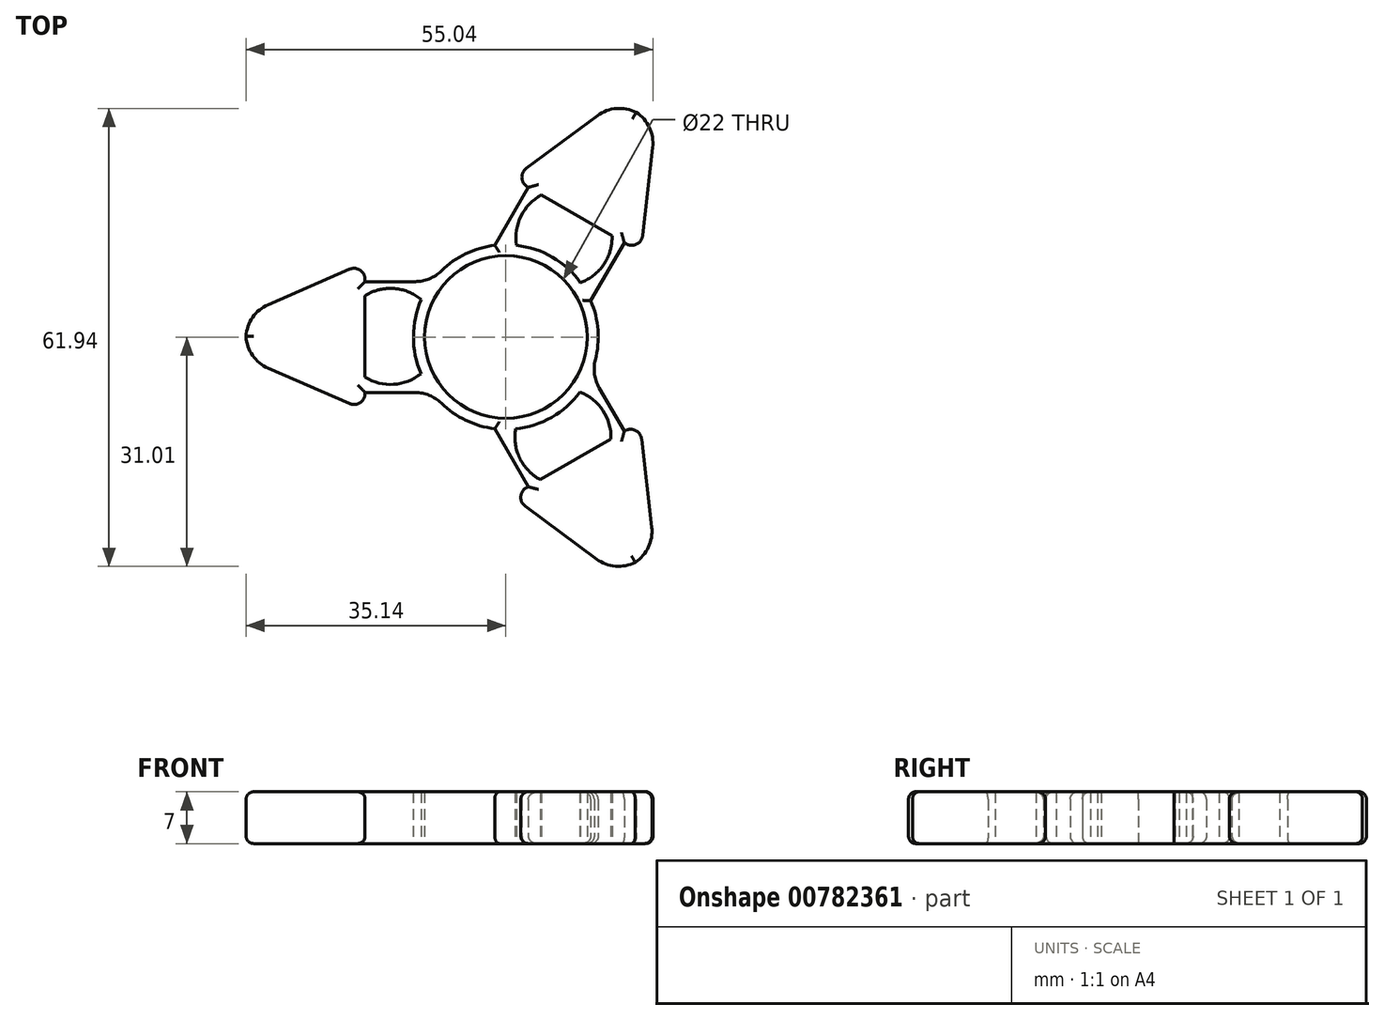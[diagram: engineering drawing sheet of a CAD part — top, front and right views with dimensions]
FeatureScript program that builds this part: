
annotation { "Feature Type Name" : "Feature", "Feature Type Description" : "" }
export const myFeature = defineFeature(function(context is Context, id is Id, definition is map)
    precondition{}
    {
        {
            var Q0;
            Q0=qCreatedBy(makeId("Top.planeOp"),FACE);
            var sketch = newSketch(context, id + "F0", { "sketchPlane" : qUnion([Q0])});
            skArc(sketch, "E0", {"start": v(0, 11) * mm, "mid": v(-11, 0.08) * mm, "end": v(-0.16, -11) * mm});
            skLineSegment(sketch, "E1", {"start": v(0, 11) * mm, "end": v(0, 55) * mm, "construction": true});
            skLineSegment(sketch, "E2", {"start": v(0, -12.5) * mm, "end": v(0, -44.64) * mm, "construction": true});
            skLineSegment(sketch, "E3", {"start": v(0, 55) * mm, "end": v(-40, 55) * mm, "construction": true});
            skLineSegment(sketch, "E4", {"start": v(-40, 55) * mm, "end": v(-40, -44.64) * mm, "construction": true});
            skLineSegment(sketch, "E5", {"start": v(-11, 0.08) * mm, "end": v(-40, 0.08) * mm, "construction": true});
            skLineSegment(sketch, "E6", {"start": v(-35.15, 0.08) * mm, "end": v(-35.15, 3.08) * mm});
            skLineSegment(sketch, "E7", {"start": v(-35.15, 0.08) * mm, "end": v(-35.15, -2.92) * mm});
            skLineSegment(sketch, "E8", {"start": v(-19.05, 0.08) * mm, "end": v(-19.05, 10.08) * mm});
            skLineSegment(sketch, "E9", {"start": v(-19.05, 0.08) * mm, "end": v(-19.05, -9.92) * mm});
            skLineSegment(sketch, "E10", {"start": v(-19.05, 10.08) * mm, "end": v(-35.15, 3.08) * mm});
            skLineSegment(sketch, "E11", {"start": v(-19.05, -9.92) * mm, "end": v(-35.15, -2.92) * mm});
            skLineSegment(sketch, "E12", {"start": v(-8.05, 7.5) * mm, "end": v(-8.05, -7.5) * mm, "construction": true});
            skLineSegment(sketch, "E13", {"start": v(-10, 7.5) * mm, "end": v(-19.05, 7.5) * mm});
            skLineSegment(sketch, "E14", {"start": v(-10, -7.5) * mm, "end": v(-19.05, -7.5) * mm});
            skPoint(sketch, "E15", {"position": v(-15.6, 0.08) * mm});
            skArc(sketch, "E16", {"start": v(-19.05, -5.43) * mm, "mid": v(-15.19, -6.4) * mm, "end": v(-11.48, -4.94) * mm});
            skArc(sketch, "E17.trimOffspring", {"start": v(-11.43, 5.06) * mm, "mid": v(-15.15, 6.57) * mm, "end": v(-19.05, 5.6) * mm});
            skArc(sketch, "E18", {"start": v(0, 12.5) * mm, "mid": v(-5.6, 11.18) * mm, "end": v(-10, 7.5) * mm});
            skLineSegment(sketch, "E19", {"start": v(0, 11) * mm, "end": v(0, 12.5) * mm});
            skArc(sketch, "E20.trimOffspring", {"start": v(-10, -7.5) * mm, "mid": v(-5.6, -11.18) * mm, "end": v(0, -12.5) * mm});
            skArc(sketch, "E21", {"start": v(-11.43, 5.06) * mm, "mid": v(-12.5, 0.07) * mm, "end": v(-11.48, -4.94) * mm});
            skPoint(sketch, "E22.orphan", {"position": v(0, -12.13) * mm});
            skLineSegment(sketch, "E23", {"start": v(-0.16, -11) * mm, "end": v(0, -12.5) * mm});
            skSolve(sketch);
        }
        {
            var Q0;
            Q0=qCreatedBy(makeId("Front.planeOp"),FACE);
            var sketch = newSketch(context, id + "F1", { "sketchPlane" : qUnion([Q0])});
            skLineSegment(sketch, "E24", {"start": v(0, 0) * mm, "end": v(0, 17.47) * mm, "construction": true});
            skSolve(sketch);
        }
        {
            var Q0;
            Q0=makeQuery(id+"F0.imprint","IMPRINT",FACE,{"disambiguationData":[TD([[makeQuery(id+"F0.imprint","IMPRINT",EDGE,{"derivedFrom":sQuery(id+"F0.wireOp",EDGE,"E6")}),-1.0]])]});
            var Q1;
            {var subQ1=sQuery(id+"F0.wireOp",EDGE,"E14");Q1=makeQuery(id+"F0.imprint","IMPRINT",FACE,{"disambiguationData":[TD([[makeQuery(id+"F0.imprint","IMPRINT",EDGE,{"derivedFrom":subQ1}),-1.0]])]});}
            var Q2;
            {var subQ0=sQuery(id+"F0.wireOp",EDGE,"E13");Q2=makeQuery(id+"F0.imprint","IMPRINT",FACE,{"disambiguationData":[TD([[makeQuery(id+"F0.imprint","IMPRINT",EDGE,{"derivedFrom":subQ0}),1.0]])]});}
            extrude(context, id + "F2", {"entities" : qUnion([Q0, Q1, Q2]), "depth" : 7 * mm, "offsetDistance" : 25 * mm});
        }
        {
            var Q0;
            Q0=makeQuery(id+"F2.opExtrude","SWEPT_BODY",BODY,{"disambiguationData":[OSD([sQuery(id+"F0.wireOp",EDGE,"E0"),sQuery(id+"F0.wireOp",EDGE,"E6"),sQuery(id+"F0.wireOp",EDGE,"E7"),sQuery(id+"F0.wireOp",EDGE,"E8"),sQuery(id+"F0.wireOp",EDGE,"E9"),sQuery(id+"F0.wireOp",EDGE,"E10"),sQuery(id+"F0.wireOp",EDGE,"E11"),sQuery(id+"F0.wireOp",EDGE,"E13"),sQuery(id+"F0.wireOp",EDGE,"E14"),sQuery(id+"F0.wireOp",EDGE,"E16"),sQuery(id+"F0.wireOp",EDGE,"E17.trimOffspring"),sQuery(id+"F0.wireOp",EDGE,"E18"),sQuery(id+"F0.wireOp",EDGE,"YHqfrzSo-FMoi-PR9p-TX1y-DZj2c1Ndsbw0"),sQuery(id+"F0.wireOp",EDGE,"E19"),sQuery(id+"F0.wireOp",EDGE,"E20.trimOffspring")])]});
            var Q1;
            Q1=sQuery(id+"F1.wireOp",EDGE,"E24");
            circularPattern(context, id + "F3", {"operationType" : NewBodyOperationType.ADD, "entities" : qUnion([Q0]), "axis" : qUnion([Q1]), "angle" : 240 * degree, "instanceCount" : 3, "equalSpace" : true});
        }
        {
            var Q0;
            Q0=makeQuery(id+"F2.opExtrude","SWEPT_EDGE",EDGE,{"disambiguationData":[OSD([sQuery(id+"F0.wireOp",EDGE,"E9"),sQuery(id+"F0.wireOp",EDGE,"E11")])]});
            var Q1;
            Q1=makeQuery(id+"F3.opPattern","COPY",EDGE,{"derivedFrom":makeQuery(id+"F2.opExtrude","SWEPT_EDGE",EDGE,{"disambiguationData":[OSD([sQuery(id+"F0.wireOp",EDGE,"E8"),sQuery(id+"F0.wireOp",EDGE,"E10")])]}),"instanceName":"1"});
            var Q2;
            Q2=makeQuery(id+"F2.opExtrude","SWEPT_EDGE",EDGE,{"disambiguationData":[OSD([sQuery(id+"F0.wireOp",EDGE,"E8"),sQuery(id+"F0.wireOp",EDGE,"E10")])]});
            var Q3;
            Q3=makeQuery(id+"F3.opPattern","COPY",EDGE,{"derivedFrom":makeQuery(id+"F2.opExtrude","SWEPT_EDGE",EDGE,{"disambiguationData":[OSD([sQuery(id+"F0.wireOp",EDGE,"E9"),sQuery(id+"F0.wireOp",EDGE,"E11")])]}),"instanceName":"1"});
            var Q4;
            Q4=makeQuery(id+"F3.opPattern","COPY",EDGE,{"derivedFrom":makeQuery(id+"F2.opExtrude","SWEPT_EDGE",EDGE,{"disambiguationData":[OSD([sQuery(id+"F0.wireOp",EDGE,"E8"),sQuery(id+"F0.wireOp",EDGE,"E10")])]}),"instanceName":"2"});
            var Q5;
            Q5=makeQuery(id+"F3.opPattern","COPY",EDGE,{"derivedFrom":makeQuery(id+"F2.opExtrude","SWEPT_EDGE",EDGE,{"disambiguationData":[OSD([sQuery(id+"F0.wireOp",EDGE,"E9"),sQuery(id+"F0.wireOp",EDGE,"E11")])]}),"instanceName":"2"});
            fillet(context, id + "F4", {"entities" : qUnion([Q0, Q1, Q2, Q3, Q4, Q5]), "radius" : 1.5 * mm, "tangentPropagation" : true, "allowEdgeOverflow" : false});
        }
        {
            var Q0;
            Q0=makeQuery(id+"F2.opExtrude","SWEPT_EDGE",EDGE,{"disambiguationData":[OSD([sQuery(id+"F0.wireOp",EDGE,"E14"),sQuery(id+"F0.wireOp",EDGE,"E20.trimOffspring")])]});
            var Q1;
            Q1=makeQuery(id+"F3.opPattern","COPY",EDGE,{"derivedFrom":makeQuery(id+"F2.opExtrude","SWEPT_EDGE",EDGE,{"disambiguationData":[OSD([sQuery(id+"F0.wireOp",EDGE,"E13"),sQuery(id+"F0.wireOp",EDGE,"E18")])]}),"instanceName":"1"});
            var Q2;
            Q2=makeQuery(id+"F3.opPattern","COPY",EDGE,{"derivedFrom":makeQuery(id+"F2.opExtrude","SWEPT_EDGE",EDGE,{"disambiguationData":[OSD([sQuery(id+"F0.wireOp",EDGE,"E14"),sQuery(id+"F0.wireOp",EDGE,"E20.trimOffspring")])]}),"instanceName":"1"});
            var Q3;
            Q3=makeQuery(id+"F3.opPattern","COPY",EDGE,{"derivedFrom":makeQuery(id+"F2.opExtrude","SWEPT_EDGE",EDGE,{"disambiguationData":[OSD([sQuery(id+"F0.wireOp",EDGE,"E13"),sQuery(id+"F0.wireOp",EDGE,"E18")])]}),"instanceName":"2"});
            var Q4;
            Q4=makeQuery(id+"F2.opExtrude","SWEPT_EDGE",EDGE,{"disambiguationData":[OSD([sQuery(id+"F0.wireOp",EDGE,"E13"),sQuery(id+"F0.wireOp",EDGE,"E18")])]});
            var Q5;
            Q5=makeQuery(id+"F3.opPattern","COPY",EDGE,{"derivedFrom":makeQuery(id+"F2.opExtrude","SWEPT_EDGE",EDGE,{"disambiguationData":[OSD([sQuery(id+"F0.wireOp",EDGE,"E14"),sQuery(id+"F0.wireOp",EDGE,"E20.trimOffspring")])]}),"instanceName":"2"});
            fillet(context, id + "F5", {"entities" : qUnion([Q0, Q1, Q2, Q3, Q4, Q5]), "radius" : 5 * mm, "tangentPropagation" : true, "allowEdgeOverflow" : false});
        }
        {
            var Q0;
            Q0=makeQuery(id+"F2.opExtrude","SWEPT_EDGE",EDGE,{"disambiguationData":[OSD([sQuery(id+"F0.wireOp",EDGE,"E7"),sQuery(id+"F0.wireOp",EDGE,"E11")])]});
            var Q1;
            Q1=makeQuery(id+"F2.opExtrude","SWEPT_EDGE",EDGE,{"disambiguationData":[OSD([sQuery(id+"F0.wireOp",EDGE,"E6"),sQuery(id+"F0.wireOp",EDGE,"E10")])]});
            var Q2;
            Q2=makeQuery(id+"F3.opPattern","COPY",EDGE,{"derivedFrom":makeQuery(id+"F2.opExtrude","SWEPT_EDGE",EDGE,{"disambiguationData":[OSD([sQuery(id+"F0.wireOp",EDGE,"E7"),sQuery(id+"F0.wireOp",EDGE,"E11")])]}),"instanceName":"2"});
            var Q3;
            Q3=makeQuery(id+"F3.opPattern","COPY",EDGE,{"derivedFrom":makeQuery(id+"F2.opExtrude","SWEPT_EDGE",EDGE,{"disambiguationData":[OSD([sQuery(id+"F0.wireOp",EDGE,"E6"),sQuery(id+"F0.wireOp",EDGE,"E10")])]}),"instanceName":"2"});
            var Q4;
            Q4=makeQuery(id+"F3.opPattern","COPY",EDGE,{"derivedFrom":makeQuery(id+"F2.opExtrude","SWEPT_EDGE",EDGE,{"disambiguationData":[OSD([sQuery(id+"F0.wireOp",EDGE,"E7"),sQuery(id+"F0.wireOp",EDGE,"E11")])]}),"instanceName":"1"});
            var Q5;
            Q5=makeQuery(id+"F3.opPattern","COPY",EDGE,{"derivedFrom":makeQuery(id+"F2.opExtrude","SWEPT_EDGE",EDGE,{"disambiguationData":[OSD([sQuery(id+"F0.wireOp",EDGE,"E6"),sQuery(id+"F0.wireOp",EDGE,"E10")])]}),"instanceName":"1"});
            fillet(context, id + "F6", {"entities" : qUnion([Q0, Q1, Q2, Q3, Q4, Q5]), "radius" : 5 * mm, "tangentPropagation" : true, "allowEdgeOverflow" : false});
        }
        {
            var Q0;
            Q0=makeQuery(id+"F2.opExtrude","CAP_EDGE",EDGE,{"disambiguationData":[OSD([sQuery(id+"F0.wireOp",EDGE,"E10")])],"isStart":false});
            var Q1;
            {var subQ0=sQuery(id+"F0.wireOp",EDGE,"E10");var subQ1=sQuery(id+"F0.wireOp",EDGE,"E6");var subQ2=makeQuery(id+"F2.opExtrude","CAP_FACE",FACE,{"disambiguationData":[OSD([sQuery(id+"F0.wireOp",EDGE,"E0"),subQ1,sQuery(id+"F0.wireOp",EDGE,"E7"),sQuery(id+"F0.wireOp",EDGE,"E8"),sQuery(id+"F0.wireOp",EDGE,"E9"),subQ0,sQuery(id+"F0.wireOp",EDGE,"E11"),sQuery(id+"F0.wireOp",EDGE,"E13"),sQuery(id+"F0.wireOp",EDGE,"E14"),sQuery(id+"F0.wireOp",EDGE,"E16"),sQuery(id+"F0.wireOp",EDGE,"E17.trimOffspring"),sQuery(id+"F0.wireOp",EDGE,"E18"),sQuery(id+"F0.wireOp",EDGE,"E19"),sQuery(id+"F0.wireOp",EDGE,"E20.trimOffspring"),sQuery(id+"F0.wireOp",EDGE,"E21"),sQuery(id+"F0.wireOp",EDGE,"E23")])],"isStart":false});Q1=makeQuery(id+"F6.opFillet","BLEND_EDGE",EDGE,{"blendedFrom":[makeQuery(id+"F2.opExtrude","SWEPT_EDGE",EDGE,{"disambiguationData":[OSD([subQ1,subQ0])]}),makeQuery(id+"F3.boolean.opBoolean","MERGE",FACE,{"derivedFrom":[subQ2,makeQuery(id+"F3.opPattern","COPY",FACE,{"derivedFrom":subQ2,"instanceName":"1"}),makeQuery(id+"F3.opPattern","COPY",FACE,{"derivedFrom":subQ2,"instanceName":"2"})]})],"blendedInto":[makeQuery(id+"F3.boolean.opBoolean","MERGE",FACE,{"derivedFrom":[subQ2,makeQuery(id+"F3.opPattern","COPY",FACE,{"derivedFrom":subQ2,"instanceName":"1"}),makeQuery(id+"F3.opPattern","COPY",FACE,{"derivedFrom":subQ2,"instanceName":"2"})]})]});}
            var Q2;
            {var subQ0=sQuery(id+"F0.wireOp",EDGE,"E11");var subQ1=sQuery(id+"F0.wireOp",EDGE,"E7");var subQ2=makeQuery(id+"F2.opExtrude","CAP_FACE",FACE,{"disambiguationData":[OSD([sQuery(id+"F0.wireOp",EDGE,"E0"),sQuery(id+"F0.wireOp",EDGE,"E6"),subQ1,sQuery(id+"F0.wireOp",EDGE,"E8"),sQuery(id+"F0.wireOp",EDGE,"E9"),sQuery(id+"F0.wireOp",EDGE,"E10"),subQ0,sQuery(id+"F0.wireOp",EDGE,"E13"),sQuery(id+"F0.wireOp",EDGE,"E14"),sQuery(id+"F0.wireOp",EDGE,"E16"),sQuery(id+"F0.wireOp",EDGE,"E17.trimOffspring"),sQuery(id+"F0.wireOp",EDGE,"E18"),sQuery(id+"F0.wireOp",EDGE,"E19"),sQuery(id+"F0.wireOp",EDGE,"E20.trimOffspring"),sQuery(id+"F0.wireOp",EDGE,"E21"),sQuery(id+"F0.wireOp",EDGE,"E23")])],"isStart":false});Q2=makeQuery(id+"F6.opFillet","BLEND_EDGE",EDGE,{"blendedFrom":[makeQuery(id+"F2.opExtrude","SWEPT_EDGE",EDGE,{"disambiguationData":[OSD([subQ1,subQ0])]}),makeQuery(id+"F3.boolean.opBoolean","MERGE",FACE,{"derivedFrom":[subQ2,makeQuery(id+"F3.opPattern","COPY",FACE,{"derivedFrom":subQ2,"instanceName":"1"}),makeQuery(id+"F3.opPattern","COPY",FACE,{"derivedFrom":subQ2,"instanceName":"2"})]})],"blendedInto":[makeQuery(id+"F3.boolean.opBoolean","MERGE",FACE,{"derivedFrom":[subQ2,makeQuery(id+"F3.opPattern","COPY",FACE,{"derivedFrom":subQ2,"instanceName":"1"}),makeQuery(id+"F3.opPattern","COPY",FACE,{"derivedFrom":subQ2,"instanceName":"2"})]})]});}
            var Q3;
            Q3=makeQuery(id+"F2.opExtrude","CAP_EDGE",EDGE,{"disambiguationData":[OSD([sQuery(id+"F0.wireOp",EDGE,"E11")])],"isStart":false});
            var Q4;
            Q4=makeQuery(id+"F2.opExtrude","CAP_EDGE",EDGE,{"disambiguationData":[OSD([sQuery(id+"F0.wireOp",EDGE,"E10")])],"isStart":true});
            var Q5;
            {var subQ0=sQuery(id+"F0.wireOp",EDGE,"E10");var subQ1=sQuery(id+"F0.wireOp",EDGE,"E6");var subQ2=makeQuery(id+"F2.opExtrude","CAP_FACE",FACE,{"disambiguationData":[OSD([sQuery(id+"F0.wireOp",EDGE,"E0"),subQ1,sQuery(id+"F0.wireOp",EDGE,"E7"),sQuery(id+"F0.wireOp",EDGE,"E8"),sQuery(id+"F0.wireOp",EDGE,"E9"),subQ0,sQuery(id+"F0.wireOp",EDGE,"E11"),sQuery(id+"F0.wireOp",EDGE,"E13"),sQuery(id+"F0.wireOp",EDGE,"E14"),sQuery(id+"F0.wireOp",EDGE,"E16"),sQuery(id+"F0.wireOp",EDGE,"E17.trimOffspring"),sQuery(id+"F0.wireOp",EDGE,"E18"),sQuery(id+"F0.wireOp",EDGE,"E19"),sQuery(id+"F0.wireOp",EDGE,"E20.trimOffspring"),sQuery(id+"F0.wireOp",EDGE,"E21"),sQuery(id+"F0.wireOp",EDGE,"E23")])],"isStart":true});Q5=makeQuery(id+"F6.opFillet","BLEND_EDGE",EDGE,{"blendedFrom":[makeQuery(id+"F2.opExtrude","SWEPT_EDGE",EDGE,{"disambiguationData":[OSD([subQ1,subQ0])]}),makeQuery(id+"F3.boolean.opBoolean","MERGE",FACE,{"derivedFrom":[subQ2,makeQuery(id+"F3.opPattern","COPY",FACE,{"derivedFrom":subQ2,"instanceName":"1"}),makeQuery(id+"F3.opPattern","COPY",FACE,{"derivedFrom":subQ2,"instanceName":"2"})]})],"blendedInto":[makeQuery(id+"F3.boolean.opBoolean","MERGE",FACE,{"derivedFrom":[subQ2,makeQuery(id+"F3.opPattern","COPY",FACE,{"derivedFrom":subQ2,"instanceName":"1"}),makeQuery(id+"F3.opPattern","COPY",FACE,{"derivedFrom":subQ2,"instanceName":"2"})]})]});}
            var Q6;
            {var subQ0=sQuery(id+"F0.wireOp",EDGE,"E11");var subQ1=sQuery(id+"F0.wireOp",EDGE,"E7");var subQ2=makeQuery(id+"F2.opExtrude","CAP_FACE",FACE,{"disambiguationData":[OSD([sQuery(id+"F0.wireOp",EDGE,"E0"),sQuery(id+"F0.wireOp",EDGE,"E6"),subQ1,sQuery(id+"F0.wireOp",EDGE,"E8"),sQuery(id+"F0.wireOp",EDGE,"E9"),sQuery(id+"F0.wireOp",EDGE,"E10"),subQ0,sQuery(id+"F0.wireOp",EDGE,"E13"),sQuery(id+"F0.wireOp",EDGE,"E14"),sQuery(id+"F0.wireOp",EDGE,"E16"),sQuery(id+"F0.wireOp",EDGE,"E17.trimOffspring"),sQuery(id+"F0.wireOp",EDGE,"E18"),sQuery(id+"F0.wireOp",EDGE,"E19"),sQuery(id+"F0.wireOp",EDGE,"E20.trimOffspring"),sQuery(id+"F0.wireOp",EDGE,"E21"),sQuery(id+"F0.wireOp",EDGE,"E23")])],"isStart":true});Q6=makeQuery(id+"F6.opFillet","BLEND_EDGE",EDGE,{"blendedFrom":[makeQuery(id+"F2.opExtrude","SWEPT_EDGE",EDGE,{"disambiguationData":[OSD([subQ1,subQ0])]}),makeQuery(id+"F3.boolean.opBoolean","MERGE",FACE,{"derivedFrom":[subQ2,makeQuery(id+"F3.opPattern","COPY",FACE,{"derivedFrom":subQ2,"instanceName":"1"}),makeQuery(id+"F3.opPattern","COPY",FACE,{"derivedFrom":subQ2,"instanceName":"2"})]})],"blendedInto":[makeQuery(id+"F3.boolean.opBoolean","MERGE",FACE,{"derivedFrom":[subQ2,makeQuery(id+"F3.opPattern","COPY",FACE,{"derivedFrom":subQ2,"instanceName":"1"}),makeQuery(id+"F3.opPattern","COPY",FACE,{"derivedFrom":subQ2,"instanceName":"2"})]})]});}
            var Q7;
            Q7=makeQuery(id+"F2.opExtrude","CAP_EDGE",EDGE,{"disambiguationData":[OSD([sQuery(id+"F0.wireOp",EDGE,"E11")])],"isStart":true});
            var Q8;
            Q8=makeQuery(id+"F3.opPattern","COPY",EDGE,{"derivedFrom":makeQuery(id+"F2.opExtrude","CAP_EDGE",EDGE,{"disambiguationData":[OSD([sQuery(id+"F0.wireOp",EDGE,"E11")])],"isStart":true}),"instanceName":"2"});
            var Q9;
            {var subQ0=sQuery(id+"F0.wireOp",EDGE,"E11");var subQ1=sQuery(id+"F0.wireOp",EDGE,"E7");var subQ2=makeQuery(id+"F2.opExtrude","CAP_FACE",FACE,{"disambiguationData":[OSD([sQuery(id+"F0.wireOp",EDGE,"E0"),sQuery(id+"F0.wireOp",EDGE,"E6"),subQ1,sQuery(id+"F0.wireOp",EDGE,"E8"),sQuery(id+"F0.wireOp",EDGE,"E9"),sQuery(id+"F0.wireOp",EDGE,"E10"),subQ0,sQuery(id+"F0.wireOp",EDGE,"E13"),sQuery(id+"F0.wireOp",EDGE,"E14"),sQuery(id+"F0.wireOp",EDGE,"E16"),sQuery(id+"F0.wireOp",EDGE,"E17.trimOffspring"),sQuery(id+"F0.wireOp",EDGE,"E18"),sQuery(id+"F0.wireOp",EDGE,"E19"),sQuery(id+"F0.wireOp",EDGE,"E20.trimOffspring"),sQuery(id+"F0.wireOp",EDGE,"E21"),sQuery(id+"F0.wireOp",EDGE,"E23")])],"isStart":true});Q9=makeQuery(id+"F6.opFillet","BLEND_EDGE",EDGE,{"blendedFrom":[makeQuery(id+"F3.opPattern","COPY",EDGE,{"derivedFrom":makeQuery(id+"F2.opExtrude","SWEPT_EDGE",EDGE,{"disambiguationData":[OSD([subQ1,subQ0])]}),"instanceName":"2"}),makeQuery(id+"F3.boolean.opBoolean","MERGE",FACE,{"derivedFrom":[subQ2,makeQuery(id+"F3.opPattern","COPY",FACE,{"derivedFrom":subQ2,"instanceName":"1"}),makeQuery(id+"F3.opPattern","COPY",FACE,{"derivedFrom":subQ2,"instanceName":"2"})]})],"blendedInto":[makeQuery(id+"F3.boolean.opBoolean","MERGE",FACE,{"derivedFrom":[subQ2,makeQuery(id+"F3.opPattern","COPY",FACE,{"derivedFrom":subQ2,"instanceName":"1"}),makeQuery(id+"F3.opPattern","COPY",FACE,{"derivedFrom":subQ2,"instanceName":"2"})]})]});}
            var Q10;
            {var subQ0=sQuery(id+"F0.wireOp",EDGE,"E10");var subQ1=sQuery(id+"F0.wireOp",EDGE,"E6");var subQ2=makeQuery(id+"F2.opExtrude","CAP_FACE",FACE,{"disambiguationData":[OSD([sQuery(id+"F0.wireOp",EDGE,"E0"),subQ1,sQuery(id+"F0.wireOp",EDGE,"E7"),sQuery(id+"F0.wireOp",EDGE,"E8"),sQuery(id+"F0.wireOp",EDGE,"E9"),subQ0,sQuery(id+"F0.wireOp",EDGE,"E11"),sQuery(id+"F0.wireOp",EDGE,"E13"),sQuery(id+"F0.wireOp",EDGE,"E14"),sQuery(id+"F0.wireOp",EDGE,"E16"),sQuery(id+"F0.wireOp",EDGE,"E17.trimOffspring"),sQuery(id+"F0.wireOp",EDGE,"E18"),sQuery(id+"F0.wireOp",EDGE,"E19"),sQuery(id+"F0.wireOp",EDGE,"E20.trimOffspring"),sQuery(id+"F0.wireOp",EDGE,"E21"),sQuery(id+"F0.wireOp",EDGE,"E23")])],"isStart":true});Q10=makeQuery(id+"F6.opFillet","BLEND_EDGE",EDGE,{"blendedFrom":[makeQuery(id+"F3.opPattern","COPY",EDGE,{"derivedFrom":makeQuery(id+"F2.opExtrude","SWEPT_EDGE",EDGE,{"disambiguationData":[OSD([subQ1,subQ0])]}),"instanceName":"2"}),makeQuery(id+"F3.boolean.opBoolean","MERGE",FACE,{"derivedFrom":[subQ2,makeQuery(id+"F3.opPattern","COPY",FACE,{"derivedFrom":subQ2,"instanceName":"1"}),makeQuery(id+"F3.opPattern","COPY",FACE,{"derivedFrom":subQ2,"instanceName":"2"})]})],"blendedInto":[makeQuery(id+"F3.boolean.opBoolean","MERGE",FACE,{"derivedFrom":[subQ2,makeQuery(id+"F3.opPattern","COPY",FACE,{"derivedFrom":subQ2,"instanceName":"1"}),makeQuery(id+"F3.opPattern","COPY",FACE,{"derivedFrom":subQ2,"instanceName":"2"})]})]});}
            var Q11;
            Q11=makeQuery(id+"F3.opPattern","COPY",EDGE,{"derivedFrom":makeQuery(id+"F2.opExtrude","CAP_EDGE",EDGE,{"disambiguationData":[OSD([sQuery(id+"F0.wireOp",EDGE,"E10")])],"isStart":true}),"instanceName":"2"});
            var Q12;
            Q12=makeQuery(id+"F3.opPattern","COPY",EDGE,{"derivedFrom":makeQuery(id+"F2.opExtrude","CAP_EDGE",EDGE,{"disambiguationData":[OSD([sQuery(id+"F0.wireOp",EDGE,"E10")])],"isStart":false}),"instanceName":"2"});
            var Q13;
            {var subQ0=sQuery(id+"F0.wireOp",EDGE,"E10");var subQ1=sQuery(id+"F0.wireOp",EDGE,"E6");var subQ2=makeQuery(id+"F2.opExtrude","CAP_FACE",FACE,{"disambiguationData":[OSD([sQuery(id+"F0.wireOp",EDGE,"E0"),subQ1,sQuery(id+"F0.wireOp",EDGE,"E7"),sQuery(id+"F0.wireOp",EDGE,"E8"),sQuery(id+"F0.wireOp",EDGE,"E9"),subQ0,sQuery(id+"F0.wireOp",EDGE,"E11"),sQuery(id+"F0.wireOp",EDGE,"E13"),sQuery(id+"F0.wireOp",EDGE,"E14"),sQuery(id+"F0.wireOp",EDGE,"E16"),sQuery(id+"F0.wireOp",EDGE,"E17.trimOffspring"),sQuery(id+"F0.wireOp",EDGE,"E18"),sQuery(id+"F0.wireOp",EDGE,"E19"),sQuery(id+"F0.wireOp",EDGE,"E20.trimOffspring"),sQuery(id+"F0.wireOp",EDGE,"E21"),sQuery(id+"F0.wireOp",EDGE,"E23")])],"isStart":false});Q13=makeQuery(id+"F6.opFillet","BLEND_EDGE",EDGE,{"blendedFrom":[makeQuery(id+"F3.opPattern","COPY",EDGE,{"derivedFrom":makeQuery(id+"F2.opExtrude","SWEPT_EDGE",EDGE,{"disambiguationData":[OSD([subQ1,subQ0])]}),"instanceName":"2"}),makeQuery(id+"F3.boolean.opBoolean","MERGE",FACE,{"derivedFrom":[subQ2,makeQuery(id+"F3.opPattern","COPY",FACE,{"derivedFrom":subQ2,"instanceName":"1"}),makeQuery(id+"F3.opPattern","COPY",FACE,{"derivedFrom":subQ2,"instanceName":"2"})]})],"blendedInto":[makeQuery(id+"F3.boolean.opBoolean","MERGE",FACE,{"derivedFrom":[subQ2,makeQuery(id+"F3.opPattern","COPY",FACE,{"derivedFrom":subQ2,"instanceName":"1"}),makeQuery(id+"F3.opPattern","COPY",FACE,{"derivedFrom":subQ2,"instanceName":"2"})]})]});}
            var Q14;
            {var subQ0=sQuery(id+"F0.wireOp",EDGE,"E11");var subQ1=sQuery(id+"F0.wireOp",EDGE,"E7");var subQ2=makeQuery(id+"F2.opExtrude","CAP_FACE",FACE,{"disambiguationData":[OSD([sQuery(id+"F0.wireOp",EDGE,"E0"),sQuery(id+"F0.wireOp",EDGE,"E6"),subQ1,sQuery(id+"F0.wireOp",EDGE,"E8"),sQuery(id+"F0.wireOp",EDGE,"E9"),sQuery(id+"F0.wireOp",EDGE,"E10"),subQ0,sQuery(id+"F0.wireOp",EDGE,"E13"),sQuery(id+"F0.wireOp",EDGE,"E14"),sQuery(id+"F0.wireOp",EDGE,"E16"),sQuery(id+"F0.wireOp",EDGE,"E17.trimOffspring"),sQuery(id+"F0.wireOp",EDGE,"E18"),sQuery(id+"F0.wireOp",EDGE,"E19"),sQuery(id+"F0.wireOp",EDGE,"E20.trimOffspring"),sQuery(id+"F0.wireOp",EDGE,"E21"),sQuery(id+"F0.wireOp",EDGE,"E23")])],"isStart":false});Q14=makeQuery(id+"F6.opFillet","BLEND_EDGE",EDGE,{"blendedFrom":[makeQuery(id+"F3.opPattern","COPY",EDGE,{"derivedFrom":makeQuery(id+"F2.opExtrude","SWEPT_EDGE",EDGE,{"disambiguationData":[OSD([subQ1,subQ0])]}),"instanceName":"2"}),makeQuery(id+"F3.boolean.opBoolean","MERGE",FACE,{"derivedFrom":[subQ2,makeQuery(id+"F3.opPattern","COPY",FACE,{"derivedFrom":subQ2,"instanceName":"1"}),makeQuery(id+"F3.opPattern","COPY",FACE,{"derivedFrom":subQ2,"instanceName":"2"})]})],"blendedInto":[makeQuery(id+"F3.boolean.opBoolean","MERGE",FACE,{"derivedFrom":[subQ2,makeQuery(id+"F3.opPattern","COPY",FACE,{"derivedFrom":subQ2,"instanceName":"1"}),makeQuery(id+"F3.opPattern","COPY",FACE,{"derivedFrom":subQ2,"instanceName":"2"})]})]});}
            var Q15;
            Q15=makeQuery(id+"F3.opPattern","COPY",EDGE,{"derivedFrom":makeQuery(id+"F2.opExtrude","CAP_EDGE",EDGE,{"disambiguationData":[OSD([sQuery(id+"F0.wireOp",EDGE,"E11")])],"isStart":false}),"instanceName":"2"});
            var Q16;
            Q16=makeQuery(id+"F3.opPattern","COPY",EDGE,{"derivedFrom":makeQuery(id+"F2.opExtrude","CAP_EDGE",EDGE,{"disambiguationData":[OSD([sQuery(id+"F0.wireOp",EDGE,"E11")])],"isStart":false}),"instanceName":"1"});
            var Q17;
            Q17=makeQuery(id+"F3.opPattern","COPY",EDGE,{"derivedFrom":makeQuery(id+"F2.opExtrude","CAP_EDGE",EDGE,{"disambiguationData":[OSD([sQuery(id+"F0.wireOp",EDGE,"E11")])],"isStart":true}),"instanceName":"1"});
            var Q18;
            {var subQ0=sQuery(id+"F0.wireOp",EDGE,"E11");var subQ1=sQuery(id+"F0.wireOp",EDGE,"E7");var subQ2=makeQuery(id+"F2.opExtrude","CAP_FACE",FACE,{"disambiguationData":[OSD([sQuery(id+"F0.wireOp",EDGE,"E0"),sQuery(id+"F0.wireOp",EDGE,"E6"),subQ1,sQuery(id+"F0.wireOp",EDGE,"E8"),sQuery(id+"F0.wireOp",EDGE,"E9"),sQuery(id+"F0.wireOp",EDGE,"E10"),subQ0,sQuery(id+"F0.wireOp",EDGE,"E13"),sQuery(id+"F0.wireOp",EDGE,"E14"),sQuery(id+"F0.wireOp",EDGE,"E16"),sQuery(id+"F0.wireOp",EDGE,"E17.trimOffspring"),sQuery(id+"F0.wireOp",EDGE,"E18"),sQuery(id+"F0.wireOp",EDGE,"E19"),sQuery(id+"F0.wireOp",EDGE,"E20.trimOffspring"),sQuery(id+"F0.wireOp",EDGE,"E21"),sQuery(id+"F0.wireOp",EDGE,"E23")])],"isStart":true});Q18=makeQuery(id+"F6.opFillet","BLEND_EDGE",EDGE,{"blendedFrom":[makeQuery(id+"F3.opPattern","COPY",EDGE,{"derivedFrom":makeQuery(id+"F2.opExtrude","SWEPT_EDGE",EDGE,{"disambiguationData":[OSD([subQ1,subQ0])]}),"instanceName":"1"}),makeQuery(id+"F3.boolean.opBoolean","MERGE",FACE,{"derivedFrom":[subQ2,makeQuery(id+"F3.opPattern","COPY",FACE,{"derivedFrom":subQ2,"instanceName":"1"}),makeQuery(id+"F3.opPattern","COPY",FACE,{"derivedFrom":subQ2,"instanceName":"2"})]})],"blendedInto":[makeQuery(id+"F3.boolean.opBoolean","MERGE",FACE,{"derivedFrom":[subQ2,makeQuery(id+"F3.opPattern","COPY",FACE,{"derivedFrom":subQ2,"instanceName":"1"}),makeQuery(id+"F3.opPattern","COPY",FACE,{"derivedFrom":subQ2,"instanceName":"2"})]})]});}
            var Q19;
            {var subQ0=sQuery(id+"F0.wireOp",EDGE,"E11");var subQ1=sQuery(id+"F0.wireOp",EDGE,"E7");var subQ2=makeQuery(id+"F2.opExtrude","CAP_FACE",FACE,{"disambiguationData":[OSD([sQuery(id+"F0.wireOp",EDGE,"E0"),sQuery(id+"F0.wireOp",EDGE,"E6"),subQ1,sQuery(id+"F0.wireOp",EDGE,"E8"),sQuery(id+"F0.wireOp",EDGE,"E9"),sQuery(id+"F0.wireOp",EDGE,"E10"),subQ0,sQuery(id+"F0.wireOp",EDGE,"E13"),sQuery(id+"F0.wireOp",EDGE,"E14"),sQuery(id+"F0.wireOp",EDGE,"E16"),sQuery(id+"F0.wireOp",EDGE,"E17.trimOffspring"),sQuery(id+"F0.wireOp",EDGE,"E18"),sQuery(id+"F0.wireOp",EDGE,"E19"),sQuery(id+"F0.wireOp",EDGE,"E20.trimOffspring"),sQuery(id+"F0.wireOp",EDGE,"E21"),sQuery(id+"F0.wireOp",EDGE,"E23")])],"isStart":false});Q19=makeQuery(id+"F6.opFillet","BLEND_EDGE",EDGE,{"blendedFrom":[makeQuery(id+"F3.opPattern","COPY",EDGE,{"derivedFrom":makeQuery(id+"F2.opExtrude","SWEPT_EDGE",EDGE,{"disambiguationData":[OSD([subQ1,subQ0])]}),"instanceName":"1"}),makeQuery(id+"F3.boolean.opBoolean","MERGE",FACE,{"derivedFrom":[subQ2,makeQuery(id+"F3.opPattern","COPY",FACE,{"derivedFrom":subQ2,"instanceName":"1"}),makeQuery(id+"F3.opPattern","COPY",FACE,{"derivedFrom":subQ2,"instanceName":"2"})]})],"blendedInto":[makeQuery(id+"F3.boolean.opBoolean","MERGE",FACE,{"derivedFrom":[subQ2,makeQuery(id+"F3.opPattern","COPY",FACE,{"derivedFrom":subQ2,"instanceName":"1"}),makeQuery(id+"F3.opPattern","COPY",FACE,{"derivedFrom":subQ2,"instanceName":"2"})]})]});}
            var Q20;
            {var subQ0=sQuery(id+"F0.wireOp",EDGE,"E10");var subQ1=sQuery(id+"F0.wireOp",EDGE,"E6");var subQ2=makeQuery(id+"F2.opExtrude","CAP_FACE",FACE,{"disambiguationData":[OSD([sQuery(id+"F0.wireOp",EDGE,"E0"),subQ1,sQuery(id+"F0.wireOp",EDGE,"E7"),sQuery(id+"F0.wireOp",EDGE,"E8"),sQuery(id+"F0.wireOp",EDGE,"E9"),subQ0,sQuery(id+"F0.wireOp",EDGE,"E11"),sQuery(id+"F0.wireOp",EDGE,"E13"),sQuery(id+"F0.wireOp",EDGE,"E14"),sQuery(id+"F0.wireOp",EDGE,"E16"),sQuery(id+"F0.wireOp",EDGE,"E17.trimOffspring"),sQuery(id+"F0.wireOp",EDGE,"E18"),sQuery(id+"F0.wireOp",EDGE,"E19"),sQuery(id+"F0.wireOp",EDGE,"E20.trimOffspring"),sQuery(id+"F0.wireOp",EDGE,"E21"),sQuery(id+"F0.wireOp",EDGE,"E23")])],"isStart":false});Q20=makeQuery(id+"F6.opFillet","BLEND_EDGE",EDGE,{"blendedFrom":[makeQuery(id+"F3.opPattern","COPY",EDGE,{"derivedFrom":makeQuery(id+"F2.opExtrude","SWEPT_EDGE",EDGE,{"disambiguationData":[OSD([subQ1,subQ0])]}),"instanceName":"1"}),makeQuery(id+"F3.boolean.opBoolean","MERGE",FACE,{"derivedFrom":[subQ2,makeQuery(id+"F3.opPattern","COPY",FACE,{"derivedFrom":subQ2,"instanceName":"1"}),makeQuery(id+"F3.opPattern","COPY",FACE,{"derivedFrom":subQ2,"instanceName":"2"})]})],"blendedInto":[makeQuery(id+"F3.boolean.opBoolean","MERGE",FACE,{"derivedFrom":[subQ2,makeQuery(id+"F3.opPattern","COPY",FACE,{"derivedFrom":subQ2,"instanceName":"1"}),makeQuery(id+"F3.opPattern","COPY",FACE,{"derivedFrom":subQ2,"instanceName":"2"})]})]});}
            var Q21;
            {var subQ0=sQuery(id+"F0.wireOp",EDGE,"E10");var subQ1=sQuery(id+"F0.wireOp",EDGE,"E6");var subQ2=makeQuery(id+"F2.opExtrude","CAP_FACE",FACE,{"disambiguationData":[OSD([sQuery(id+"F0.wireOp",EDGE,"E0"),subQ1,sQuery(id+"F0.wireOp",EDGE,"E7"),sQuery(id+"F0.wireOp",EDGE,"E8"),sQuery(id+"F0.wireOp",EDGE,"E9"),subQ0,sQuery(id+"F0.wireOp",EDGE,"E11"),sQuery(id+"F0.wireOp",EDGE,"E13"),sQuery(id+"F0.wireOp",EDGE,"E14"),sQuery(id+"F0.wireOp",EDGE,"E16"),sQuery(id+"F0.wireOp",EDGE,"E17.trimOffspring"),sQuery(id+"F0.wireOp",EDGE,"E18"),sQuery(id+"F0.wireOp",EDGE,"E19"),sQuery(id+"F0.wireOp",EDGE,"E20.trimOffspring"),sQuery(id+"F0.wireOp",EDGE,"E21"),sQuery(id+"F0.wireOp",EDGE,"E23")])],"isStart":true});Q21=makeQuery(id+"F6.opFillet","BLEND_EDGE",EDGE,{"blendedFrom":[makeQuery(id+"F3.opPattern","COPY",EDGE,{"derivedFrom":makeQuery(id+"F2.opExtrude","SWEPT_EDGE",EDGE,{"disambiguationData":[OSD([subQ1,subQ0])]}),"instanceName":"1"}),makeQuery(id+"F3.boolean.opBoolean","MERGE",FACE,{"derivedFrom":[subQ2,makeQuery(id+"F3.opPattern","COPY",FACE,{"derivedFrom":subQ2,"instanceName":"1"}),makeQuery(id+"F3.opPattern","COPY",FACE,{"derivedFrom":subQ2,"instanceName":"2"})]})],"blendedInto":[makeQuery(id+"F3.boolean.opBoolean","MERGE",FACE,{"derivedFrom":[subQ2,makeQuery(id+"F3.opPattern","COPY",FACE,{"derivedFrom":subQ2,"instanceName":"1"}),makeQuery(id+"F3.opPattern","COPY",FACE,{"derivedFrom":subQ2,"instanceName":"2"})]})]});}
            var Q22;
            Q22=makeQuery(id+"F3.opPattern","COPY",EDGE,{"derivedFrom":makeQuery(id+"F2.opExtrude","CAP_EDGE",EDGE,{"disambiguationData":[OSD([sQuery(id+"F0.wireOp",EDGE,"E10")])],"isStart":false}),"instanceName":"1"});
            var Q23;
            Q23=makeQuery(id+"F3.opPattern","COPY",EDGE,{"derivedFrom":makeQuery(id+"F2.opExtrude","CAP_EDGE",EDGE,{"disambiguationData":[OSD([sQuery(id+"F0.wireOp",EDGE,"E10")])],"isStart":true}),"instanceName":"1"});
            fillet(context, id + "F7", {"entities" : qUnion([Q0, Q1, Q2, Q3, Q4, Q5, Q6, Q7, Q8, Q9, Q10, Q11, Q12, Q13, Q14, Q15, Q16, Q17, Q18, Q19, Q20, Q21, Q22, Q23]), "radius" : 1 * mm, "tangentPropagation" : true, "allowEdgeOverflow" : false});
        }
        {
            var Q0;
            Q0=makeQuery(id+"F3.opPattern","COPY",EDGE,{"derivedFrom":makeQuery(id+"F2.opExtrude","CAP_EDGE",EDGE,{"disambiguationData":[OSD([sQuery(id+"F0.wireOp",EDGE,"E14")])],"isStart":false}),"instanceName":"1"});
            var Q1;
            Q1=makeQuery(id+"F3.opPattern","COPY",EDGE,{"derivedFrom":makeQuery(id+"F2.opExtrude","CAP_EDGE",EDGE,{"disambiguationData":[OSD([sQuery(id+"F0.wireOp",EDGE,"E14")])],"isStart":true}),"instanceName":"1"});
            var Q2;
            Q2=makeQuery(id+"F3.opPattern","COPY",EDGE,{"derivedFrom":makeQuery(id+"F2.opExtrude","CAP_EDGE",EDGE,{"disambiguationData":[OSD([sQuery(id+"F0.wireOp",EDGE,"E14")])],"isStart":false}),"instanceName":"2"});
            var Q3;
            Q3=makeQuery(id+"F3.opPattern","COPY",EDGE,{"derivedFrom":makeQuery(id+"F2.opExtrude","CAP_EDGE",EDGE,{"disambiguationData":[OSD([sQuery(id+"F0.wireOp",EDGE,"E14")])],"isStart":true}),"instanceName":"2"});
            var Q4;
            Q4=makeQuery(id+"F2.opExtrude","CAP_EDGE",EDGE,{"disambiguationData":[OSD([sQuery(id+"F0.wireOp",EDGE,"E13")])],"isStart":false});
            var Q5;
            Q5=makeQuery(id+"F2.opExtrude","CAP_EDGE",EDGE,{"disambiguationData":[OSD([sQuery(id+"F0.wireOp",EDGE,"E13")])],"isStart":true});
            var Q6;
            Q6=makeQuery(id+"F2.opExtrude","CAP_EDGE",EDGE,{"disambiguationData":[OSD([sQuery(id+"F0.wireOp",EDGE,"E14")])],"isStart":true});
            var Q7;
            Q7=makeQuery(id+"F2.opExtrude","CAP_EDGE",EDGE,{"disambiguationData":[OSD([sQuery(id+"F0.wireOp",EDGE,"E14")])],"isStart":false});
            var Q8;
            Q8=makeQuery(id+"F3.opPattern","COPY",EDGE,{"derivedFrom":makeQuery(id+"F2.opExtrude","CAP_EDGE",EDGE,{"disambiguationData":[OSD([sQuery(id+"F0.wireOp",EDGE,"E13")])],"isStart":false}),"instanceName":"1"});
            var Q9;
            Q9=makeQuery(id+"F3.opPattern","COPY",EDGE,{"derivedFrom":makeQuery(id+"F2.opExtrude","CAP_EDGE",EDGE,{"disambiguationData":[OSD([sQuery(id+"F0.wireOp",EDGE,"E13")])],"isStart":true}),"instanceName":"1"});
            var Q10;
            Q10=makeQuery(id+"F3.opPattern","COPY",EDGE,{"derivedFrom":makeQuery(id+"F2.opExtrude","CAP_EDGE",EDGE,{"disambiguationData":[OSD([sQuery(id+"F0.wireOp",EDGE,"E13")])],"isStart":true}),"instanceName":"2"});
            var Q11;
            Q11=makeQuery(id+"F3.opPattern","COPY",EDGE,{"derivedFrom":makeQuery(id+"F2.opExtrude","CAP_EDGE",EDGE,{"disambiguationData":[OSD([sQuery(id+"F0.wireOp",EDGE,"E13")])],"isStart":false}),"instanceName":"2"});
            fillet(context, id + "F8", {"entities" : qUnion([Q0, Q1, Q2, Q3, Q4, Q5, Q6, Q7, Q8, Q9, Q10, Q11]), "radius" : 1 * mm, "tangentPropagation" : true, "allowEdgeOverflow" : false});
        }
    });
